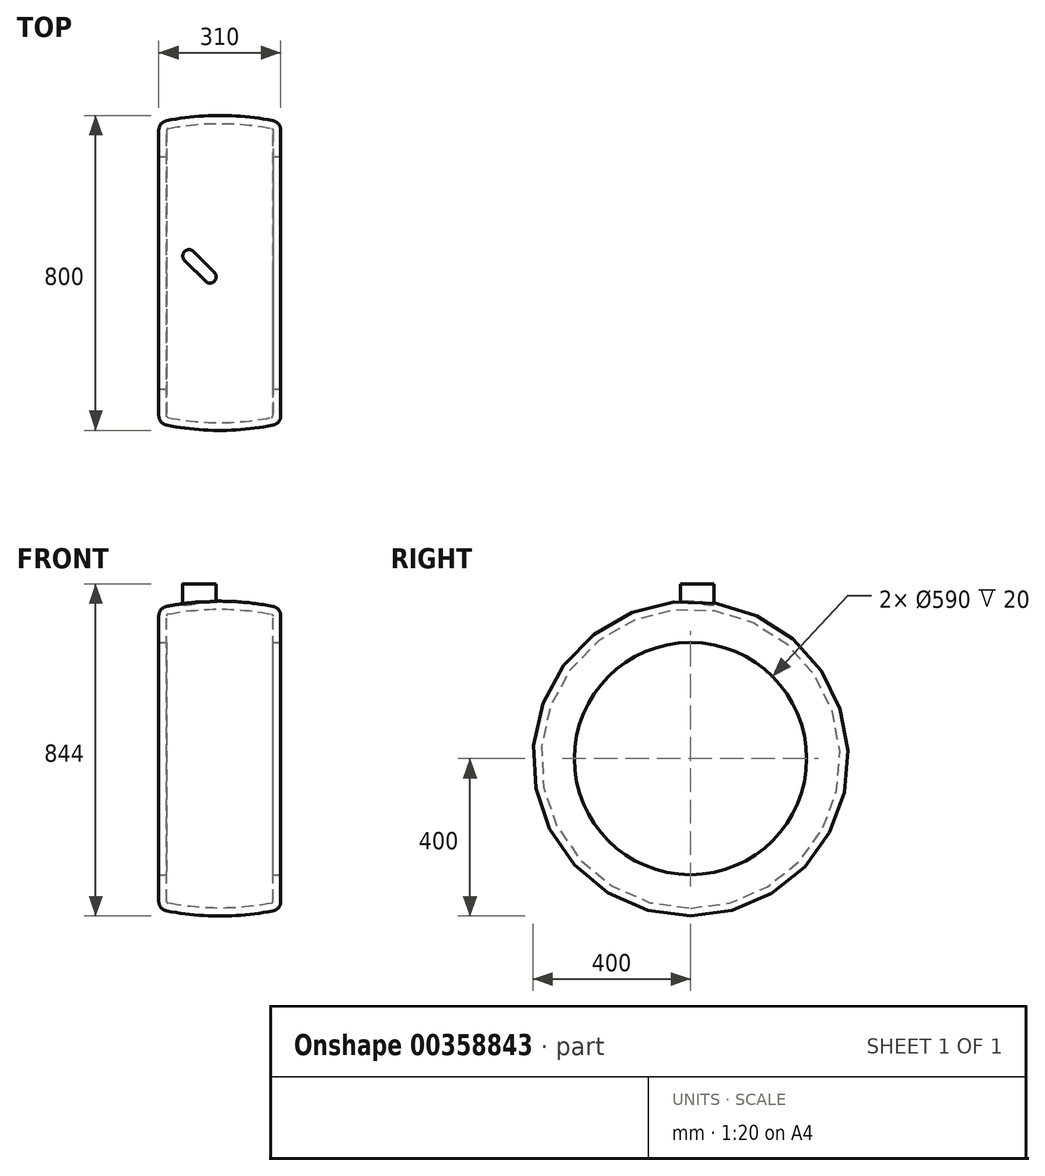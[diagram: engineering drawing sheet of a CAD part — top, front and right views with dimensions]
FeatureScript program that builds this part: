
annotation { "Feature Type Name" : "Feature", "Feature Type Description" : "" }
export const myFeature = defineFeature(function(context is Context, id is Id, definition is map)
    precondition{}
    {
        {
            var Q0;
            Q0=qCreatedBy(makeId("Front.planeOp"),FACE);
            var sketch = newSketch(context, id + "F0", { "sketchPlane" : qUnion([Q0])});
            skLineSegment(sketch, "E0", {"start": v(155, 295) * mm, "end": v(155, 362.36) * mm});
            skLineSegment(sketch, "E1", {"start": v(-155, 362.36) * mm, "end": v(-155, 295) * mm});
            skLineSegment(sketch, "E2", {"start": v(155, 295) * mm, "end": v(-155, 295) * mm});
            skArc(sketch, "E3", {"start": v(134.81, 386.9) * mm, "mid": v(0, 400) * mm, "end": v(-134.81, 386.9) * mm});
            skPoint(sketch, "E4.orphan", {"position": v(-155, 0) * mm});
            skPoint(sketch, "E5.orphan", {"position": v(155, 0) * mm});
            skPoint(sketch, "E6.visualSharp", {"position": v(155, 382.62) * mm});
            skArc(sketch, "E6.filletArc", {"start": v(155, 362.36) * mm, "mid": v(149.3, 378.25) * mm, "end": v(134.81, 386.9) * mm});
            skPoint(sketch, "E7.visualSharp", {"position": v(-155, 382.62) * mm});
            skArc(sketch, "E7.filletArc", {"start": v(-134.81, 386.9) * mm, "mid": v(-149.3, 378.25) * mm, "end": v(-155, 362.36) * mm});
            skLineSegment(sketch, "E8", {"start": v(99.3, 0) * mm, "end": v(-133.28, 0) * mm, "construction": true});
            skSolve(sketch);
        }
        {
            var Q0;
            Q0=makeQuery(id+"F0.imprint","IMPRINT",FACE,{"disambiguationData":[TD([[makeQuery(id+"F0.imprint","IMPRINT",EDGE,{"derivedFrom":sQuery(id+"F0.wireOp",EDGE,"E0")}),1.0]])]});
            var Q1;
            Q1=sQuery(id+"F0.wireOp",EDGE,"E8");
            revolve(context, id + "F1", {"entities" : qUnion([Q0]), "axis" : qUnion([Q1]), "revolveType" : RevolveType.FULL});
        }
        {
            var Q0;
            Q0=makeQuery(id+"F1.opRevolve","SWEPT_FACE",FACE,{"disambiguationData":[OSD([sQuery(id+"F0.wireOp",EDGE,"E2")])]});
            shell(context, id + "F2", {"entities" : qUnion([Q0]), "thickness" : 20 * mm});
        }
        {
            var Q0;
            Q0=qCreatedBy(makeId("Top.planeOp"),FACE);
            cPlane(context, id + "F3", {"entities" : qUnion([Q0]), "cplaneType" : CPlaneType.OFFSET, "offset" : 444 * mm, "width" : 150 * mm, "height" : 150 * mm});
        }
        {
            var Q0;
            Q0=qCreatedBy(id+"F3.planeOp",FACE);
            var sketch = newSketch(context, id + "F4", { "sketchPlane" : qUnion([Q0])});
            skLineSegment(sketch, "E9", {"start": v(0, -131.55) * mm, "end": v(0, 126.66) * mm, "construction": true});
            skArc(sketch, "E10", {"start": v(-36.31, -21.17) * mm, "mid": v(-13.69, -21.17) * mm, "end": v(-13.69, 1.46) * mm});
            skArc(sketch, "E11", {"start": v(-66.72, 54.5) * mm, "mid": v(-89.35, 54.5) * mm, "end": v(-89.35, 31.86) * mm});
            skLineSegment(sketch, "E12", {"start": v(-13.69, 1.46) * mm, "end": v(-66.72, 54.5) * mm});
            skLineSegment(sketch, "E13", {"start": v(-36.31, -21.17) * mm, "end": v(-89.35, 31.86) * mm});
            skSolve(sketch);
        }
        {
            var Q0;
            Q0=makeQuery(id+"F4.imprint","IMPRINT",FACE,{"disambiguationData":[TD([[makeQuery(id+"F4.imprint","IMPRINT",EDGE,{"derivedFrom":sQuery(id+"F4.wireOp",EDGE,"E10")}),1.0]])]});
            var Q1;
            Q1=makeQuery(id+"F1.opRevolve","SWEPT_FACE",FACE,{"disambiguationData":[OSD([sQuery(id+"F0.wireOp",EDGE,"E3")])]});
            extrude(context, id + "F5", {"entities" : qUnion([Q0]), "endBound" : BoundingType.UP_TO_SURFACE, "oppositeDirection" : true, "endBoundEntityFace" : qUnion([Q1]), "depth" : 25 * mm});
        }
    });
